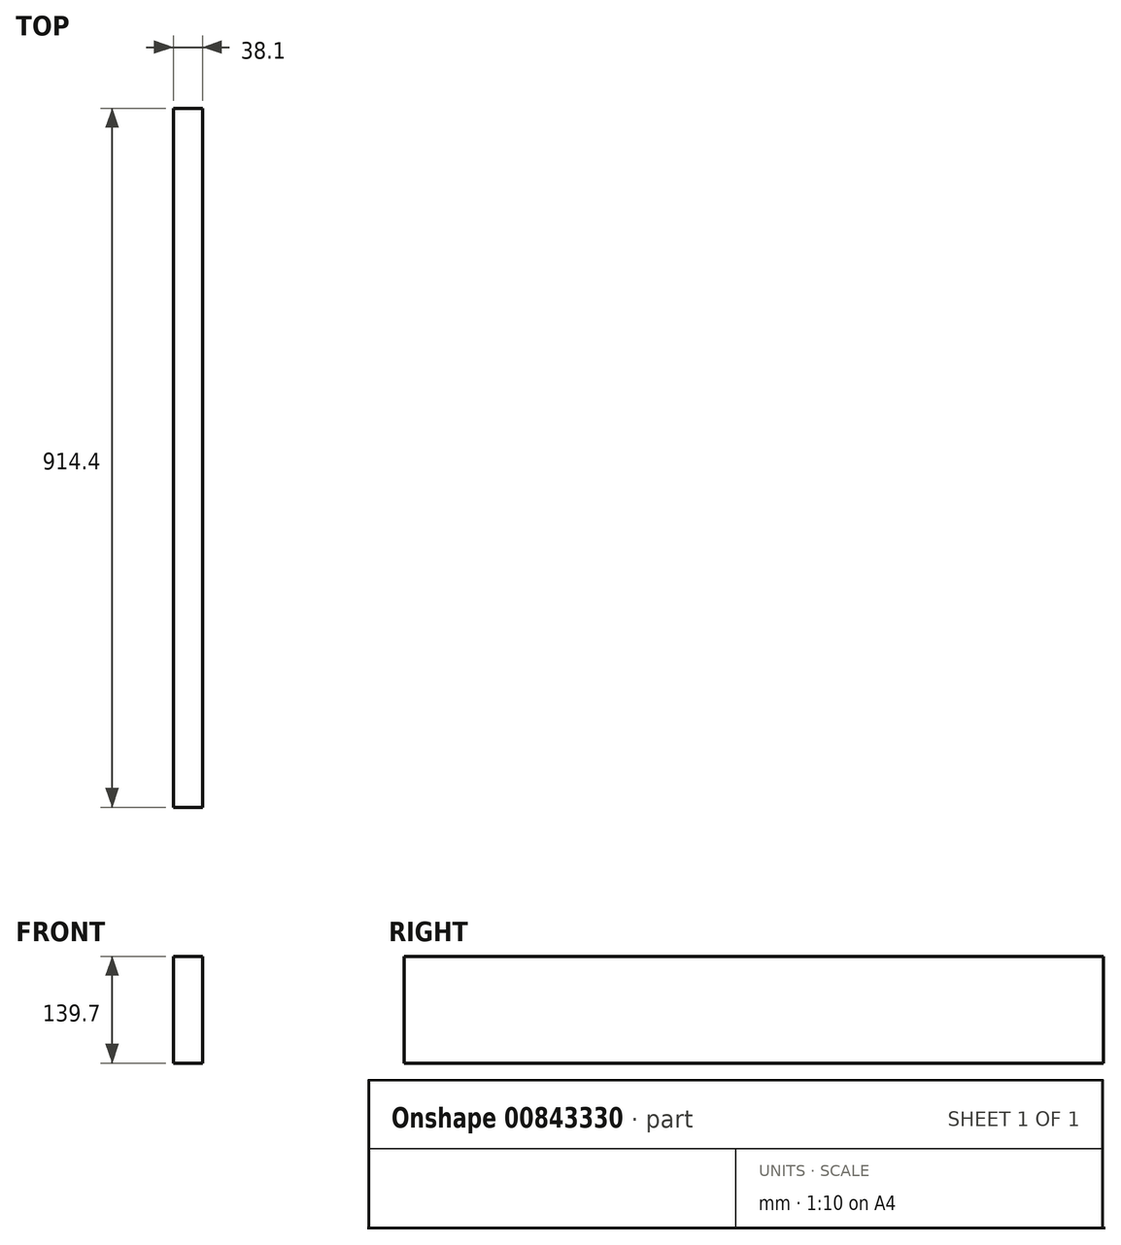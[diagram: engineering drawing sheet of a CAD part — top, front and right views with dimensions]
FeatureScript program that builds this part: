
annotation { "Feature Type Name" : "Feature", "Feature Type Description" : "" }
export const myFeature = defineFeature(function(context is Context, id is Id, definition is map)
    precondition{}
    {
        {
            var Q0;
            Q0=qCreatedBy(makeId("Front.planeOp"),FACE);
            var sketch = newSketch(context, id + "F0", { "sketchPlane" : qUnion([Q0])});
            skLineSegment(sketch, "E0.bottom", {"start": v(19.05, -69.85) * mm, "end": v(-19.05, -69.85) * mm});
            skLineSegment(sketch, "E0.top", {"start": v(19.05, 69.85) * mm, "end": v(-19.05, 69.85) * mm});
            skLineSegment(sketch, "E0.left", {"start": v(19.05, -69.85) * mm, "end": v(19.05, 69.85) * mm});
            skLineSegment(sketch, "E0.right", {"start": v(-19.05, -69.85) * mm, "end": v(-19.05, 69.85) * mm});
            skPoint(sketch, "E0.middle", {"position": v(0, 0) * mm});
            skSolve(sketch);
        }
        {
            var Q0;
            Q0 = qSketchRegion(id + "F0", true);
            extrude(context, id + "F1", {"entities" : qUnion([Q0]), "depth" : 914.4 * mm, "offsetDistance" : 25.4 * mm});
        }
    });
